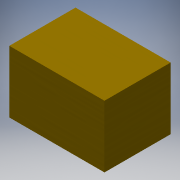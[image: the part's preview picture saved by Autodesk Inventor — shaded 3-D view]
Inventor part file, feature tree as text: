
AUTODESK INVENTOR PART (.ipt)
format: ipt  version: 2017 (Build 210142000, 142)  size: 94,208 bytes
history: native  units: mm
features: other x4, reference x2, extrude x1, sketch x1
ambient origin geometry x8: Origin, YZ Plane, XZ Plane, XY Plane, X Axis, Y Axis, Z Axis, Center Point
bodies: Solid1 (feature_tree)
feature tree (8):
  extrude  "Extrusion1"  Depth=150.0mm TaperAngle=0.0deg
  sketch  "Sketch1"  dims[d0=230.0mm d1=150.0mm d2=0.0mm]
  reference  "Reference1"
  reference  "Reference2"
  other  "<userpath>\OneDrive\Inventor\VolledigGeassembleerdv001.iam"
  other  "VolledigGeassembleerdv001.iam"
  other  "Frame:1"
  other  "aandrijfMotor:1"
